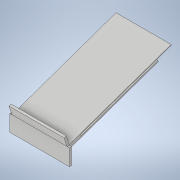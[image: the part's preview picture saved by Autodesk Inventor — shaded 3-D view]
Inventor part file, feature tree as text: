
AUTODESK INVENTOR PART (.ipt)
format: ipt  version: 2021 (Build 250183000, 183)  size: 236,032 bytes
history: native  units: mm
features: sketch x11, extrude x10, hole x1
ambient origin geometry x8: Origin, YZ Plane, XZ Plane, XY Plane, X Axis, Y Axis, Z Axis, Center Point
bodies: 实体1 (feature_tree)
feature tree (22):
  extrude  "拉伸1"  Depth=3.0mm
  extrude  "拉伸3"  Depth=74.0mm TaperAngle=0.0deg
  extrude  "拉伸4"  Depth=3.0mm
  extrude  "拉伸5"  Depth=1.0mm
  extrude  "拉伸7"  Depth=2.3mm
  extrude  "拉伸8"  Depth=1.0mm
  extrude  "拉伸9"  Depth=15.0mm
  hole  "孔1"  [1 undecoded]
  extrude  "拉伸14"  Depth=5.0mm
  sketch  "草图22"  dims[d33=100.0mm d34=0.0mm d35=3.0mm]
  extrude  "拉伸15"  Depth=3.0mm
  extrude  "拉伸16"  Depth=3.0mm TaperAngle=0.0deg
  sketch  "草图1"  dims[d1=3.0mm d2=19.078194mm]
  sketch  "草图4"  dims[d3=138.2mm d5=74.0mm d6=0.0mm]
  sketch  "草图5"  dims[d10=5.0mm d11=3.0mm]
  sketch  "草图6"  dims[d12=13.0mm d13=0.0mm d15=1.0mm]
  sketch  "草图8"  dims[d16=150.0mm d17=2.3mm]
  sketch  "草图9"  dims[d18=5.0mm d19=0.0mm d20=1.0mm]
  sketch  "草图10"  dims[d21=2.3mm d22=15.0mm]
  sketch  "草图11"  dims[d23=15.0mm d24=150.0mm]
  sketch  "草图21"  dims[d25=5.0mm d26=0.0mm d32=20.0mm]
  sketch  "草图25"  dims[d36=3.0mm d37=3.0mm d38=0.0mm d39=1.5mm d40=10.0mm d42=10.0mm d43=0.0mm d44=18.0mm d45=18.0mm d46=2.013mm d47=2.0mm d48=4.0mm d49=2.0mm d50=90.0deg d51=2.0mm d52=20.594885mm d53=7.0mm d54=7.0mm d55=10.0mm d56=3.0mm d57=8.0mm d58=6.0mm d72=150.0mm d73=0.0mm d74=10.0mm d75=10.0mm d76=5.0mm d78=2.5mm d79=0.0mm d81=1.7mm d82=0.0mm d90=22.0mm d70=0.5mm d71=0.872665mm]
note: 1 required parameter value undecoded (feature->parameter linkage not recoverable at this tier; creation-order binding heuristic only, values carry confidence <= 0.55)
